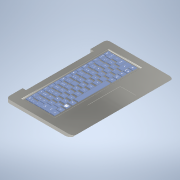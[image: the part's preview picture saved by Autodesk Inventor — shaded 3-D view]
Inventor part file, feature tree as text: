
AUTODESK INVENTOR PART (.ipt)
format: ipt  version: 2022 (Build 260153000, 153)  size: 4,612,608 bytes
history: native  units: mm
features: sketch x14, extrude x14, fillet x4, plane x1, loft x1, direct_edit x1, other x1
ambient origin geometry x8: Origin, YZ Plane, XZ Plane, XY Plane, X Axis, Y Axis, Z Axis, Center Point
bodies: Solid1 (feature_tree)
feature tree (36):
  sketch  "Sketch1"  dims[d0=20.0mm d1=30.0mm]
  plane  "Work Plane1"
  loft  "Loft1"
  extrude  "Extrusion1"  Depth=19.0mm
  fillet  "Fillet1"  Radius=30.0mm
  fillet  "Fillet2"  [1 undecoded]
  extrude  "Extrusion2"  Depth=20.0mm
  fillet  "Fillet3"  Radius=1.0mm
  extrude  "Extrusion3"  Depth=1.0mm TaperAngle=0.0deg
  fillet  "Fillet4"  Radius=1.0mm
  extrude  "Extrusion4"  Depth=5.0mm
  extrude  "Extrusion5"  Depth=10.0mm
  extrude  "Extrusion6"  Depth=0.1mm TaperAngle=0.0deg
  sketch  "Sketch10"  dims[d24=26.0mm d25=2.0mm]
  sketch  "Sketch11"  dims[d26=1.5mm d27=0.25mm d28=0.0mm]
  sketch  "Sketch12"  dims[d29=0.5mm d30=0.75mm]
  sketch  "Sketch13"  dims[d31=1.5mm d32=0.267mm]
  sketch  "Sketch14"  dims[d33=0.25mm d34=150.0mm d36=1.65mm d37=10.0mm d39=10.0mm]
  sketch  "Sketch15"  dims[d41=0.25mm d42=0.0mm d43=1.3mm d44=1.1mm d45=0.25mm d46=0.25mm d47=1.3mm d48=1.4mm d49=1.3mm d50=2.0mm d51=1.3mm d52=2.5mm d53=1.3mm d54=1.6mm d55=0.25mm d56=0.25mm d57=0.25mm d58=0.25mm d59=0.25mm d60=0.25mm d61=0.25mm d62=0.0mm d63=1.3mm d64=1.3mm d65=0.25mm d66=0.5mm d67=120.0mm d69=1.8mm d70=10.0mm d72=10.0mm d74=1.3mm d75=1.667mm d76=0.25mm d77=0.25mm d78=1.3mm d79=1.3mm d80=0.25mm d81=0.25mm d82=130.0mm d84=1.80558mm d85=10.0mm d87=10.0mm d89=1.3mm d90=1.3mm d91=0.25mm d92=0.25mm d93=110.0mm d95=1.85mm d96=10.0mm d98=10.0mm d100=1.3mm d101=2.067mm d102=0.5mm d103=0.25mm d104=1.3mm d105=1.3mm d106=0.25mm d107=0.25mm d108=100.0mm d110=1.9mm d111=10.0mm d113=10.0mm d115=1.3mm d116=2.967mm d117=0.5mm d118=0.25mm d119=1.3mm d120=1.3mm d121=0.25mm d122=0.25mm d123=30.0mm d125=1.75mm d126=10.0mm d128=10.0mm d130=1.3mm d131=1.3mm d132=0.0mm d133=0.25mm d134=0.6mm d135=1.3mm d136=0.6mm d137=1.3mm d138=0.05mm d139=0.0mm d140=0.25mm d141=0.25mm d142=1.3mm d143=1.3mm d144=0.25mm d145=0.25mm d146=1.3mm d147=1.3mm d148=1.3mm d149=1.3mm d150=0.25mm d151=0.25mm d152=0.25mm d153=0.25mm d154=1.3mm d155=9.5mm d156=0.25mm d157=0.4835mm d158=0.2mm d159=0.0mm d160=0.65mm d161=0.9mm d162=0.8mm d163=0.25mm d164=0.2mm d165=0.05mm d166=0.05mm d167=0.3mm d168=0.225mm d169=0.15mm d170=0.460703mm d171=0.043633mm d172=0.5mm d173=0.5mm d174=0.4mm d175=0.4mm d176=0.3mm d177=0.05mm d178=0.025mm d179=0.075mm d180=0.075mm d181=0.075mm d182=0.075mm d183=0.001mm d184=0.0mm d185=0.001mm d186=0.0mm d187=0.001mm d188=0.0mm d189=0.001mm d190=0.0mm d191=0.001mm d192=0.0mm d193=0.001mm d194=0.0mm d195=0.001mm d196=0.0mm d197=0.001mm d198=0.0mm d199=5.0mm d200=10.0mm d201=10.0mm d202=0.0mm]
  extrude  "Extrusion7"  Depth=10.0mm
  extrude  "Extrusion8"  Depth=2.0mm
  extrude  "Extrusion9"  Depth=0.25mm TaperAngle=0.0deg
  extrude  "Extrusion10"  Depth=0.75mm
  extrude  "Extrusion11"  Depth=0.267mm
  extrude  "Extrusion12"  Depth=150.0mm
  extrude  "Extrusion13"  Depth=1.3mm
  extrude  "Extrusion14"  Depth=1.1mm
  direct_edit  "Direct Edit1"
  sketch  "Sketch2"  dims[d2=-1.0mm d3=19.0mm d4=30.0mm d5=0.0mm d6=90.0deg]
  sketch  "Sketch3"  dims[d7=0.0mm d8=90.0deg d9=20.0mm d10=1.0mm]
  sketch  "Sketch5"  dims[d11=5.0mm d12=1.0mm d13=0.0mm d14=1.0mm]
  sketch  "Sketch6"  dims[d15=0.1mm d16=5.0mm]
  sketch  "Sketch7"  dims[d17=10.0mm d18=10.0mm]
  sketch  "Sketch8"  dims[d19=1.0mm d20=0.1mm d21=0.0mm]
  sketch  "Sketch9"  dims[d22=0.5mm d23=10.0mm]
  other  "Scale1"
note: 1 required parameter value undecoded (feature->parameter linkage not recoverable at this tier; creation-order binding heuristic only, values carry confidence <= 0.55)
